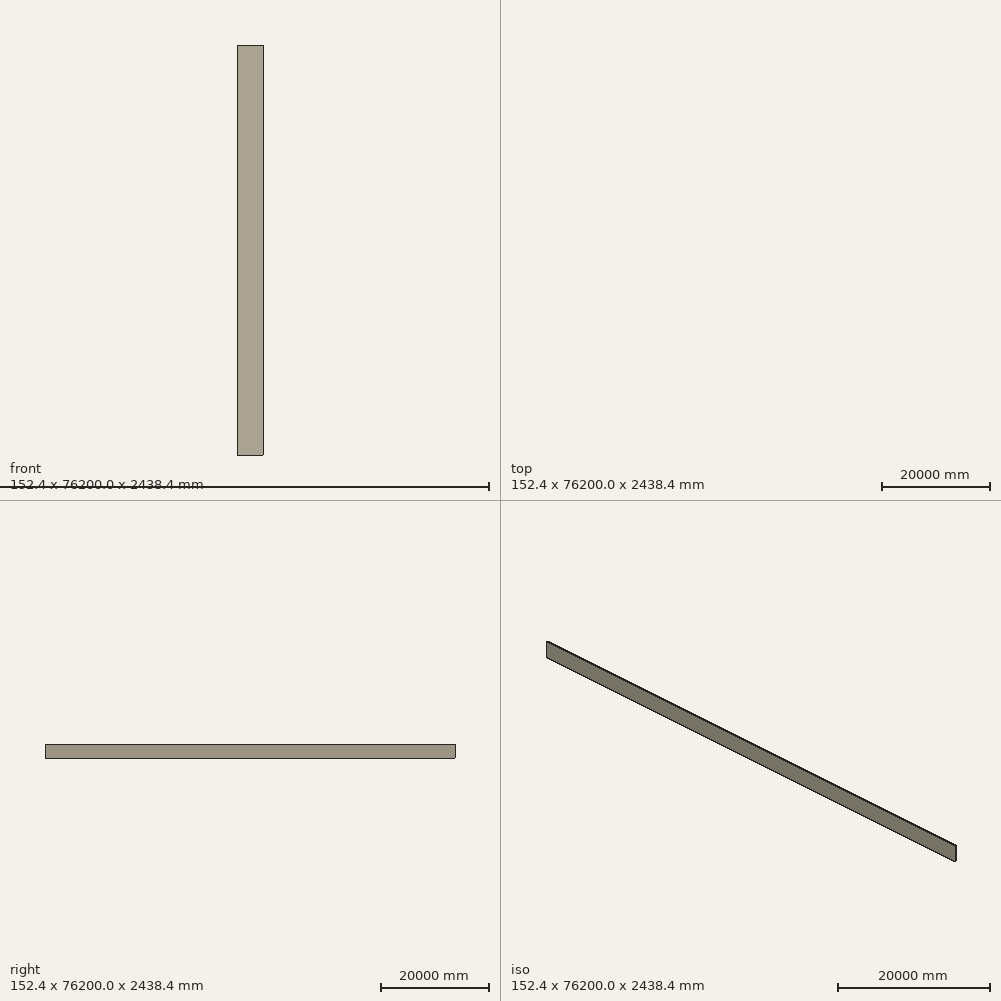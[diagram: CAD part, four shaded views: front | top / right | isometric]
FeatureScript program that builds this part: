
annotation { "Feature Type Name" : "Feature", "Feature Type Description" : "" }
export const myFeature = defineFeature(function(context is Context, id is Id, definition is map)
    precondition{}
    {
        {
            var Q0;
            Q0=qCreatedBy(makeId("Top.planeOp"),FACE);
            var sketch = newSketch(context, id + "F0", { "sketchPlane" : qUnion([Q0])});
            skLineSegment(sketch, "E0", {"start": v(0, 0) * mm, "end": v(0, 67056) * mm});
            skSolve(sketch);
        }
        {
            var Q0;
            Q0=qCreatedBy(makeId("Top.planeOp"),FACE);
            var sketch = newSketch(context, id + "F1", { "sketchPlane" : qUnion([Q0])});
            skLineSegment(sketch, "E1", {"start": v(0, 0) * mm, "end": v(0, 76200) * mm});
            skLineSegment(sketch, "E2.0", {"start": v(6.35, 0) * mm, "end": v(6.35, 76200) * mm});
            skLineSegment(sketch, "E3.0", {"start": v(152.4, 0) * mm, "end": v(152.4, 76200) * mm});
            skLineSegment(sketch, "E4", {"start": v(0, 76200) * mm, "end": v(152.4, 76200) * mm});
            skLineSegment(sketch, "E5", {"start": v(0, 0) * mm, "end": v(152.4, 0) * mm});
            skSolve(sketch);
        }
        {
            var Q0;
            {var subQ0=sQuery(id+"F1.wireOp",EDGE,"E2.0");Q0=makeQuery(id+"F1.imprint","IMPRINT",FACE,{"disambiguationData":[TD([[makeQuery(id+"F1.imprint","IMPRINT",EDGE,{"derivedFrom":subQ0}),-1.0]])]});}
            var Q1;
            {var subQ0=sQuery(id+"F1.wireOp",EDGE,"E1");Q1=makeQuery(id+"F1.imprint","IMPRINT",FACE,{"disambiguationData":[TD([[makeQuery(id+"F1.imprint","IMPRINT",EDGE,{"derivedFrom":subQ0}),-1.0]])]});}
            extrude(context, id + "F2", {"entities" : qUnion([Q0, Q1]), "depth" : 2438.4 * mm});
        }
    });
